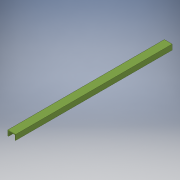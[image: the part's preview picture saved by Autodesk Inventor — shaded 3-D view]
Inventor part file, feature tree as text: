
AUTODESK INVENTOR PART (.ipt)
format: ipt  version: 2017 SP1 (Build 210196100, 196)  size: 100,352 bytes
history: native  units: in
note: dims shown in document units (in); Inventor stores cm internally (conversion verified against a paired STEP export)
features: extrude x1, sketch x1
ambient origin geometry x8: Origin, YZ Plane, XZ Plane, XY Plane, X Axis, Y Axis, Z Axis, Center Point
bodies: Solid1 (feature_tree)
feature tree (2):
  extrude  "Extrusion1"  Depth=1.25in
  sketch  "Sketch1"  dims[d0=0.125in d1=1.25in d2=1.0in d3=1.5in d4=30.0in d5=0.0in]
